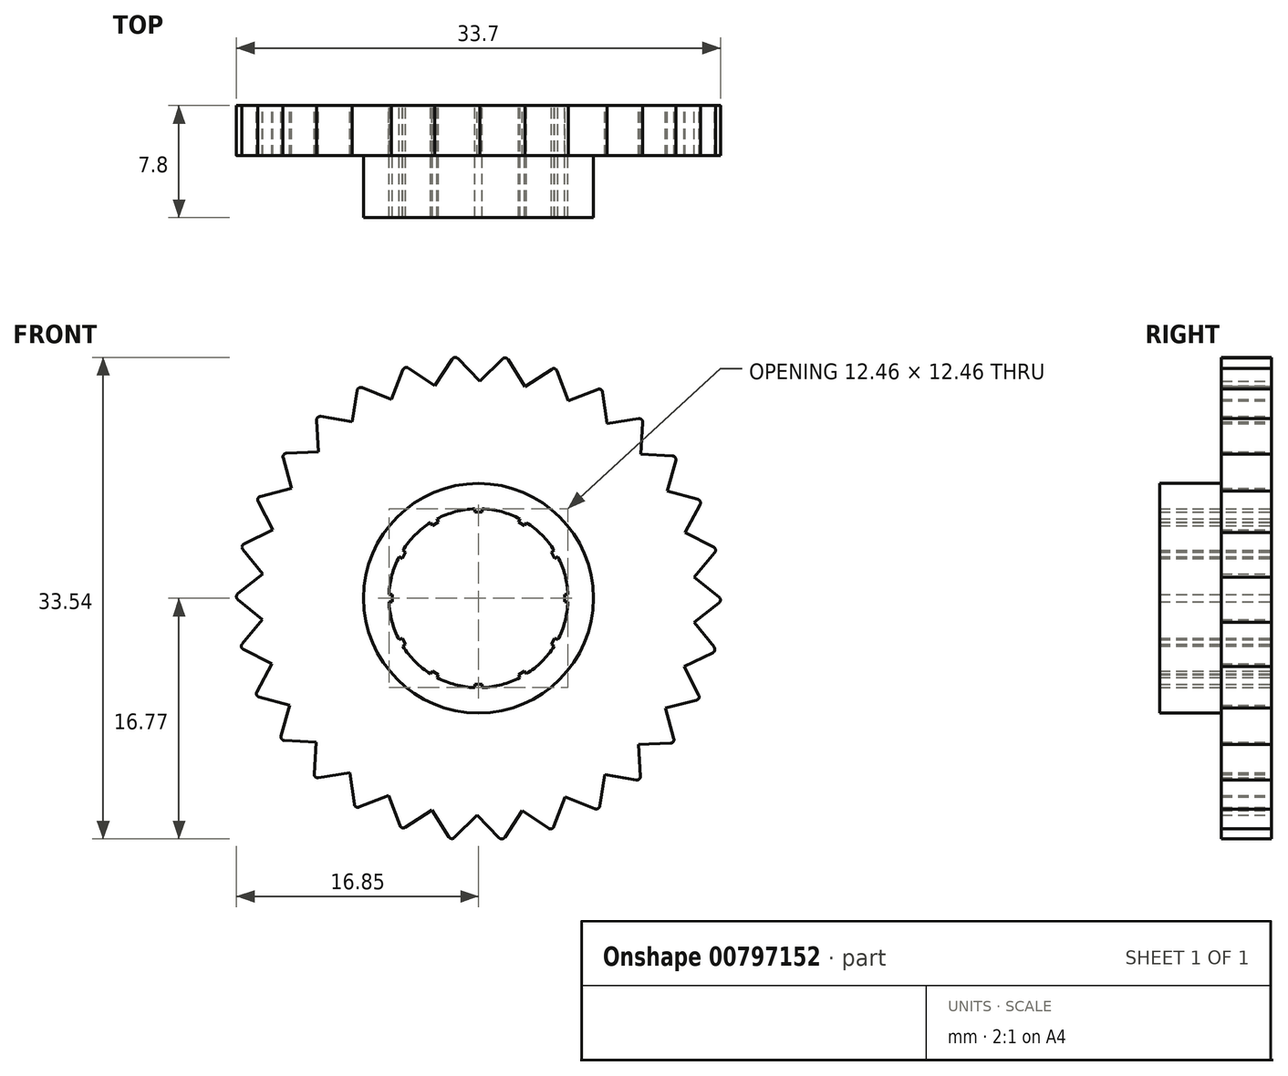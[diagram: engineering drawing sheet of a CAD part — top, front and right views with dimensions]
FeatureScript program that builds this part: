
annotation { "Feature Type Name" : "Feature", "Feature Type Description" : "" }
export const myFeature = defineFeature(function(context is Context, id is Id, definition is map)
    precondition{}
    {
        {
            var Q0;
            Q0=qCreatedBy(makeId("Front.planeOp"),FACE);
            var sketch = newSketch(context, id + "F0", { "sketchPlane" : qUnion([Q0])});
            skCircle(sketch, "E0", {"center": v(0, 0) * mm, "radius": 15 * mm});
            skCircle(sketch, "E1", {"center": v(0, 0) * mm, "radius": 8 * mm});
            skCircle(sketch, "E2", {"center": v(0, 0) * mm, "radius": 6.24 * mm});
            skLineSegment(sketch, "E3", {"start": v(0.25, 6.23) * mm, "end": v(0.25, 6) * mm});
            skLineSegment(sketch, "E4", {"start": v(0.25, 6) * mm, "end": v(-0.25, 6) * mm});
            skLineSegment(sketch, "E5", {"start": v(-0.25, 6) * mm, "end": v(-0.25, 6.23) * mm});
            skSolve(sketch);
        }
        {
            var Q0;
            Q0=makeQuery(id+"F0.imprint","IMPRINT",FACE,{"disambiguationData":[TD([[makeQuery(id+"F0.imprint","IMPRINT",EDGE,{"derivedFrom":sQuery(id+"F0.wireOp",EDGE,"E1")}),1.0]])]});
            extrude(context, id + "F1", {"entities" : qUnion([Q0]), "depth" : 7.8 * mm, "offsetDistance" : 25 * mm});
        }
        {
            var Q0;
            Q0=makeQuery(id+"F0.imprint","IMPRINT",FACE,{"disambiguationData":[TD([[makeQuery(id+"F0.imprint","IMPRINT",EDGE,{"derivedFrom":sQuery(id+"F0.wireOp",EDGE,"E0")}),1.0]])]});
            extrude(context, id + "F2", {"entities" : qUnion([Q0]), "operationType" : NewBodyOperationType.ADD, "depth" : 3.5 * mm, "offsetDistance" : 25 * mm});
        }
        {
            var Q0;
            {var subQ0=sQuery(id+"F0.wireOp",EDGE,"E3");Q0=makeQuery(id+"F0.imprint","IMPRINT",FACE,{"disambiguationData":[TD([[makeQuery(id+"F0.imprint","IMPRINT",EDGE,{"derivedFrom":subQ0}),-1.0]])]});}
            extrude(context, id + "F3", {"entities" : qUnion([Q0]), "depth" : 7.8 * mm, "offsetDistance" : 25 * mm});
        }
        {
            var Q0;
            Q0=makeQuery(id+"F3.opExtrude","SWEPT_BODY",BODY,{"disambiguationData":[OSD([sQuery(id+"F0.wireOp",EDGE,"E2"),sQuery(id+"F0.wireOp",EDGE,"E3"),sQuery(id+"F0.wireOp",EDGE,"E4"),sQuery(id+"F0.wireOp",EDGE,"E5")])]});
            var Q1;
            Q1=sQuery(id+"F0.wireOp",EDGE,"E2");
            circularPattern(context, id + "F4", {"operationType" : NewBodyOperationType.ADD, "entities" : qUnion([Q0]), "axis" : qUnion([Q1]), "angle" : 360 * degree, "instanceCount" : 12, "equalSpace" : true});
        }
        {
            var Q0;
            Q0=qCreatedBy(makeId("Front.planeOp"),FACE);
            var sketch = newSketch(context, id + "F5", { "sketchPlane" : qUnion([Q0])});
            skLineSegment(sketch, "E6", {"start": v(0, 0) * mm, "end": v(0, 15) * mm, "construction": true});
            skPoint(sketch, "E7", {"position": v(0, 15) * mm});
            skLineSegment(sketch, "E8", {"start": v(0, 15) * mm, "end": v(1.9, 16.9) * mm});
            skLineSegment(sketch, "E9", {"start": v(1.9, 16.9) * mm, "end": v(3.32, 14.63) * mm});
            skArc(sketch, "E10.0", {"start": v(3.32, 14.63) * mm, "mid": v(1.67, 14.9) * mm, "end": v(0, 15) * mm});
            skSolve(sketch);
        }
        {
            var Q0;
            Q0 = qSketchRegion(id + "F5", true);
            extrude(context, id + "F6", {"entities" : qUnion([Q0]), "depth" : 3.5 * mm, "offsetDistance" : 25 * mm});
        }
        {
            var Q0;
            Q0=qCreatedBy(makeId("Right.planeOp"),FACE);
            var sketch = newSketch(context, id + "F7", { "sketchPlane" : qUnion([Q0])});
            skLineSegment(sketch, "E11", {"start": v(0, 0) * mm, "end": v(-17.9, 0) * mm, "construction": true});
            skSolve(sketch);
        }
        {
            var Q0;
            Q0=makeQuery(id+"F6.opExtrude","SWEPT_EDGE",EDGE,{"disambiguationData":[OSD([sQuery(id+"F5.wireOp",EDGE,"E8"),sQuery(id+"F5.wireOp",EDGE,"E9")])]});
            fillet(context, id + "F8", {"entities" : qUnion([Q0]), "radius" : .25 * mm, "tangentPropagation" : true, "allowEdgeOverflow" : false});
        }
        {
            var Q0;
            Q0=makeQuery(id+"F6.opExtrude","SWEPT_BODY",BODY,{"disambiguationData":[OSD([sQuery(id+"F5.wireOp",EDGE,"E8"),sQuery(id+"F5.wireOp",EDGE,"E9"),sQuery(id+"F5.wireOp",EDGE,"E10.0")])]});
            var Q1;
            Q1=sQuery(id+"F7.wireOp",EDGE,"E11");
            circularPattern(context, id + "F9", {"operationType" : NewBodyOperationType.ADD, "entities" : qUnion([Q0]), "axis" : qUnion([Q1]), "angle" : 360 * degree, "instanceCount" : 30, "equalSpace" : true});
        }
    });
